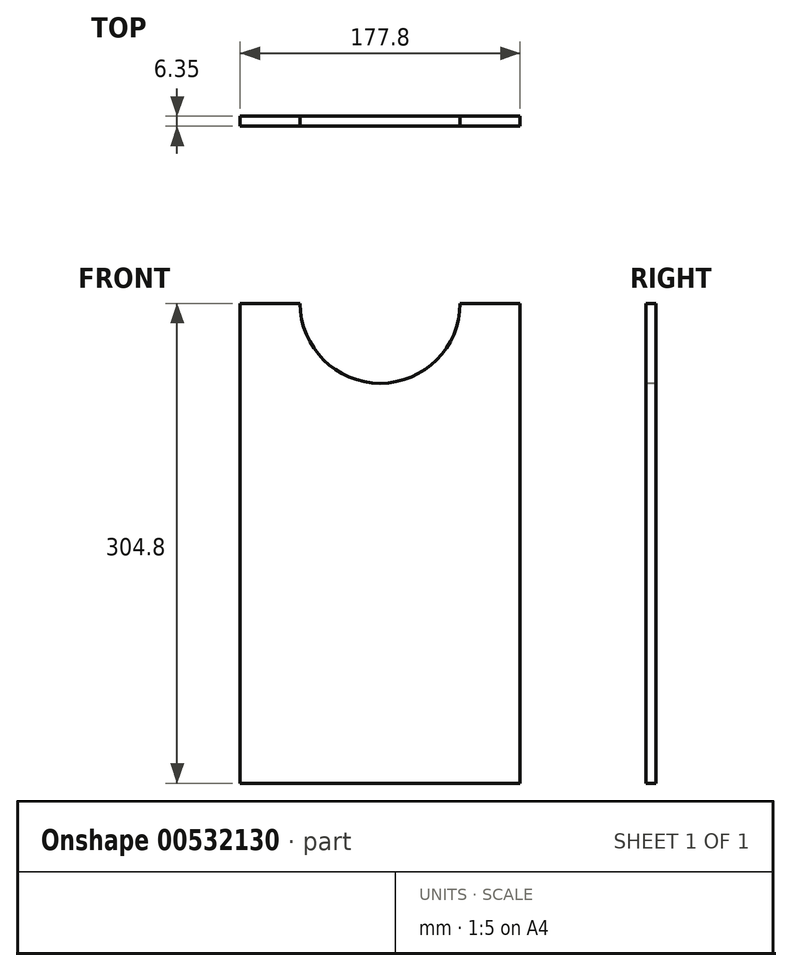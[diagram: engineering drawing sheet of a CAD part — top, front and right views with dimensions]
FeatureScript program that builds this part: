
annotation { "Feature Type Name" : "Feature", "Feature Type Description" : "" }
export const myFeature = defineFeature(function(context is Context, id is Id, definition is map)
    precondition{}
    {
        {
            var Q0;
            Q0=qCreatedBy(makeId("Front.planeOp"),FACE);
            var sketch = newSketch(context, id + "F0", { "sketchPlane" : qUnion([Q0])});
            skLineSegment(sketch, "E0.bottom", {"start": v(88.9, -152.4) * mm, "end": v(-88.9, -152.4) * mm});
            skLineSegment(sketch, "E0.top", {"start": v(88.9, 152.4) * mm, "end": v(-88.9, 152.4) * mm});
            skLineSegment(sketch, "E0.left", {"start": v(88.9, -152.4) * mm, "end": v(88.9, 152.4) * mm});
            skLineSegment(sketch, "E0.right", {"start": v(-88.9, -152.4) * mm, "end": v(-88.9, 152.4) * mm});
            skPoint(sketch, "E0.middle", {"position": v(0, 0) * mm});
            skSolve(sketch);
        }
        {
            var Q0;
            Q0 = qSketchRegion(id + "F0", true);
            extrude(context, id + "F1", {"entities" : qUnion([Q0]), "depth" : 6.35 * mm, "offsetDistance" : 25.4 * mm});
        }
        {
            var Q0;
            Q0=makeQuery(id+"F1.opExtrude","CAP_FACE",FACE,{"disambiguationData":[OSD([sQuery(id+"F0.wireOp",EDGE,"E0.bottom"),sQuery(id+"F0.wireOp",EDGE,"E0.top"),sQuery(id+"F0.wireOp",EDGE,"E0.left"),sQuery(id+"F0.wireOp",EDGE,"E0.right")])],"isStart":false});
            var sketch = newSketch(context, id + "F2", { "sketchPlane" : qUnion([Q0])});
            skPoint(sketch, "E1", {"position": v(0, 152.4) * mm});
            skArc(sketch, "E2", {"start": v(-50.8, 152.4) * mm, "mid": v(0, 101.6) * mm, "end": v(50.8, 152.4) * mm});
            skSolve(sketch);
        }
        {
            var Q0;
            Q0 = qSketchRegion(id + "F2", true);
            var Q1;
            {var subQ0=sQuery(id+"F2.wireOp",EDGE,"E2");Q1=makeQuery(id+"F2.imprint","IMPRINT",FACE,{"disambiguationData":[TD([[makeQuery(id+"F2.imprint","IMPRINT",EDGE,{"derivedFrom":subQ0}),1.0]])]});}
            extrude(context, id + "F3", {"entities" : qUnion([Q0, Q1]), "operationType" : NewBodyOperationType.REMOVE, "oppositeDirection" : true, "depth" : 25.4 * mm, "offsetDistance" : 25.4 * mm});
        }
    });
